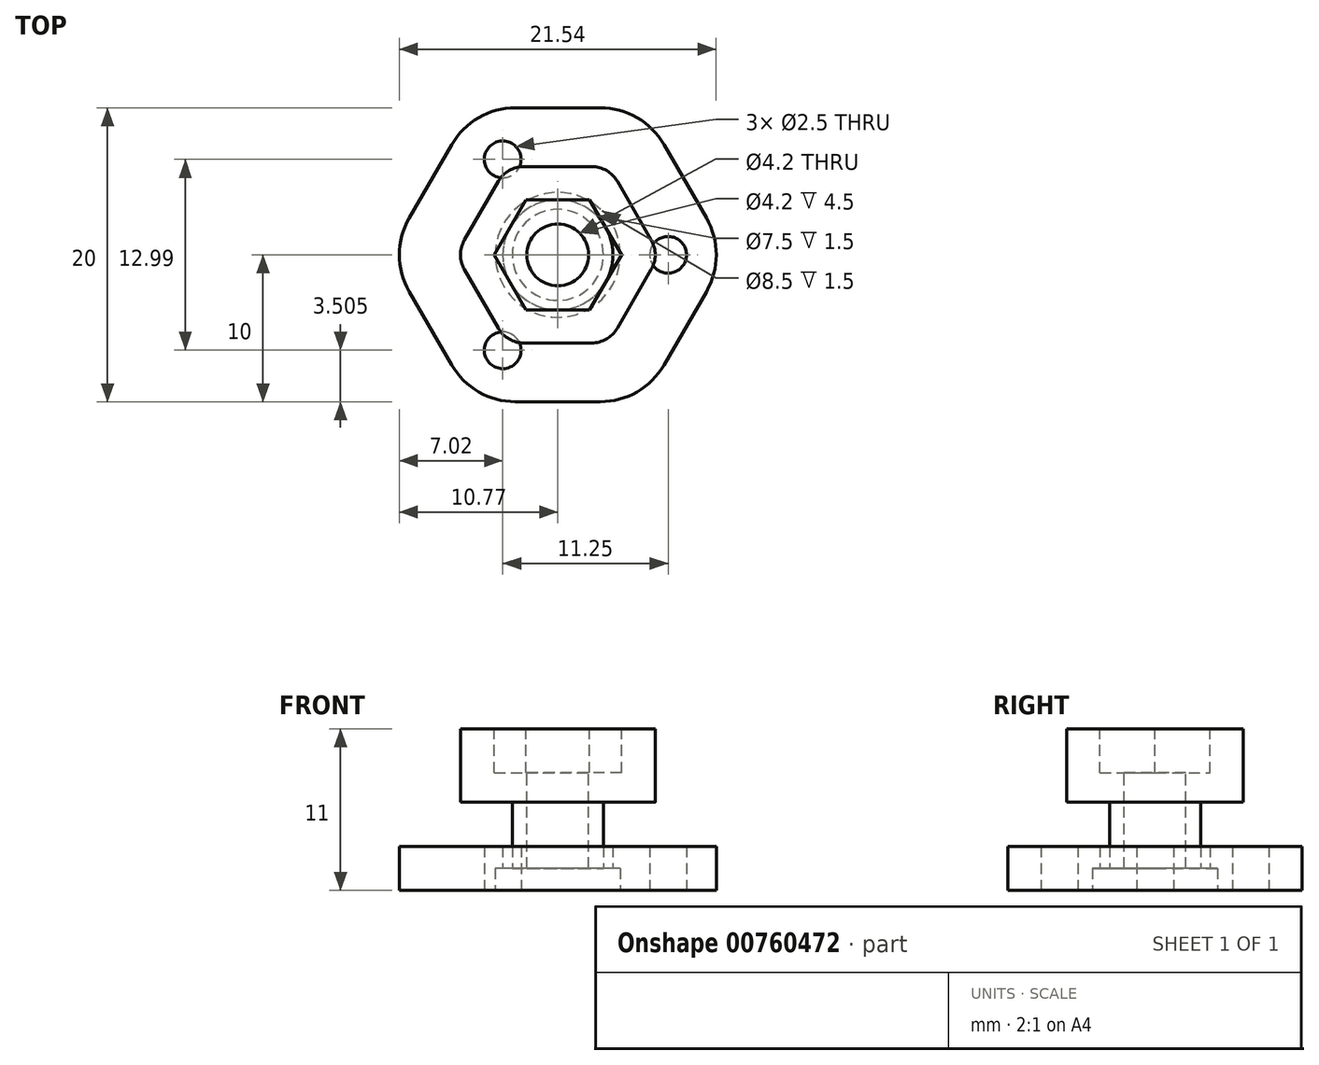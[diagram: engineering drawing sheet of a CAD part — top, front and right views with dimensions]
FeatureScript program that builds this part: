
annotation { "Feature Type Name" : "Feature", "Feature Type Description" : "" }
export const myFeature = defineFeature(function(context is Context, id is Id, definition is map)
    precondition{}
    {
        {
            var Q0;
            Q0=qCreatedBy(makeId("Top.planeOp"),FACE);
            var sketch = newSketch(context, id + "F0", { "sketchPlane" : qUnion([Q0])});
            skCircle(sketch, "E0.cCircle", {"center": v(0, 0) * mm, "radius": 10 * mm, "construction": true});
            skLineSegment(sketch, "E0.0", {"start": v(-5.77, 10) * mm, "end": v(5.77, 10) * mm});
            skLineSegment(sketch, "E0.1", {"start": v(5.77, 10) * mm, "end": v(11.55, 0) * mm});
            skLineSegment(sketch, "E0.2", {"start": v(11.55, 0) * mm, "end": v(5.77, -10) * mm});
            skLineSegment(sketch, "E0.3", {"start": v(5.77, -10) * mm, "end": v(-5.77, -10) * mm});
            skLineSegment(sketch, "E0.4", {"start": v(-5.77, -10) * mm, "end": v(-11.55, 0) * mm});
            skLineSegment(sketch, "E0.5", {"start": v(-11.55, 0) * mm, "end": v(-5.77, 10) * mm});
            skPoint(sketch, "E0.0.midPoint", {"position": v(0, 10) * mm});
            skCircle(sketch, "E1", {"center": v(0, 0) * mm, "radius": 4.25 * mm});
            skCircle(sketch, "E2", {"center": v(0, 0) * mm, "radius": 3.75 * mm});
            skCircle(sketch, "E3", {"center": v(7.5, 0) * mm, "radius": 1.25 * mm});
            skCircle(sketch, "E4.1.0", {"center": v(-3.75, 6.5) * mm, "radius": 1.25 * mm});
            skCircle(sketch, "E4.2.0", {"center": v(-3.75, -6.5) * mm, "radius": 1.25 * mm});
            skSolve(sketch);
        }
        {
            var Q0;
            Q0=makeQuery(id+"F0.imprint","IMPRINT",FACE,{"disambiguationData":[TD([[makeQuery(id+"F0.imprint","IMPRINT",EDGE,{"derivedFrom":sQuery(id+"F0.wireOp",EDGE,"E0.0")}),-1.0]])]});
            var Q1;
            Q1=makeQuery(id+"F0.imprint","IMPRINT",FACE,{"disambiguationData":[TD([[makeQuery(id+"F0.imprint","IMPRINT",EDGE,{"derivedFrom":sQuery(id+"F0.wireOp",EDGE,"E1")}),1.0]])]});
            extrude(context, id + "F1", {"entities" : qUnion([Q0, Q1]), "depth" : 3 * mm, "offsetDistance" : 25 * mm});
        }
        {
            var Q0;
            Q0=makeQuery(id+"F0.imprint","IMPRINT",FACE,{"disambiguationData":[TD([[makeQuery(id+"F0.imprint","IMPRINT",EDGE,{"derivedFrom":sQuery(id+"F0.wireOp",EDGE,"E1")}),1.0]])]});
            extrude(context, id + "F2", {"entities" : qUnion([Q0]), "operationType" : NewBodyOperationType.REMOVE, "depth" : 1.5 * mm, "offsetDistance" : 25 * mm});
        }
        {
            var Q0;
            Q0=makeQuery(id+"F1.opExtrude","SWEPT_EDGE",EDGE,{"disambiguationData":[OSD([sQuery(id+"F0.wireOp",EDGE,"E0.2"),sQuery(id+"F0.wireOp",EDGE,"E0.3")])]});
            var Q1;
            Q1=makeQuery(id+"F1.opExtrude","SWEPT_EDGE",EDGE,{"disambiguationData":[OSD([sQuery(id+"F0.wireOp",EDGE,"E0.1"),sQuery(id+"F0.wireOp",EDGE,"E0.2")])]});
            var Q2;
            Q2=makeQuery(id+"F1.opExtrude","SWEPT_EDGE",EDGE,{"disambiguationData":[OSD([sQuery(id+"F0.wireOp",EDGE,"E0.3"),sQuery(id+"F0.wireOp",EDGE,"E0.4")])]});
            var Q3;
            Q3=makeQuery(id+"F1.opExtrude","SWEPT_EDGE",EDGE,{"disambiguationData":[OSD([sQuery(id+"F0.wireOp",EDGE,"E0.4"),sQuery(id+"F0.wireOp",EDGE,"E0.5")])]});
            var Q4;
            Q4=makeQuery(id+"F1.opExtrude","SWEPT_EDGE",EDGE,{"disambiguationData":[OSD([sQuery(id+"F0.wireOp",EDGE,"E0.0"),sQuery(id+"F0.wireOp",EDGE,"E0.5")])]});
            var Q5;
            Q5=makeQuery(id+"F1.opExtrude","SWEPT_EDGE",EDGE,{"disambiguationData":[OSD([sQuery(id+"F0.wireOp",EDGE,"E0.0"),sQuery(id+"F0.wireOp",EDGE,"E0.1")])]});
            fillet(context, id + "F3", {"entities" : qUnion([Q0, Q1, Q2, Q3, Q4, Q5]), "radius" : 5 * mm, "tangentPropagation" : true, "allowEdgeOverflow" : false});
        }
        {
            var Q0;
            Q0=makeQuery(id+"F2.boolean.opBoolean","COPY",FACE,{"derivedFrom":makeQuery(id+"F2.opExtrude","CAP_FACE",FACE,{"disambiguationData":[OSD([sQuery(id+"F0.wireOp",EDGE,"E1"),sQuery(id+"F0.wireOp",EDGE,"E2")])],"isStart":false})});
            var sketch = newSketch(context, id + "F4", { "sketchPlane" : qUnion([Q0])});
            skCircle(sketch, "E5", {"center": v(0, 0) * mm, "radius": 3.1 * mm});
            skSolve(sketch);
        }
        {
            var Q0;
            Q0 = qSketchRegion(id + "F4", true);
            extrude(context, id + "F5", {"entities" : qUnion([Q0]), "oppositeDirection" : true, "depth" : 4.5 * mm, "offsetDistance" : 25 * mm});
        }
        {
            var Q0;
            Q0=makeQuery(id+"F5.opExtrude","CAP_FACE",FACE,{"disambiguationData":[OSD([sQuery(id+"F4.wireOp",EDGE,"E5")])],"isStart":false});
            var sketch = newSketch(context, id + "F6", { "sketchPlane" : qUnion([Q0])});
            skCircle(sketch, "E6.cCircle", {"center": v(0, 0) * mm, "radius": 6 * mm, "construction": true});
            skLineSegment(sketch, "E6.0", {"start": v(-3.46, 6) * mm, "end": v(3.46, 6) * mm});
            skLineSegment(sketch, "E6.1", {"start": v(3.46, 6) * mm, "end": v(6.93, 0) * mm});
            skLineSegment(sketch, "E6.2", {"start": v(6.93, 0) * mm, "end": v(3.46, -6) * mm});
            skLineSegment(sketch, "E6.3", {"start": v(3.46, -6) * mm, "end": v(-3.46, -6) * mm});
            skLineSegment(sketch, "E6.4", {"start": v(-3.46, -6) * mm, "end": v(-6.93, 0) * mm});
            skLineSegment(sketch, "E6.5", {"start": v(-6.93, 0) * mm, "end": v(-3.46, 6) * mm});
            skPoint(sketch, "E6.0.midPoint", {"position": v(0, 6) * mm});
            skSolve(sketch);
        }
        {
            var Q0;
            Q0 = qSketchRegion(id + "F6", true);
            extrude(context, id + "F7", {"entities" : qUnion([Q0]), "depth" : 5 * mm, "offsetDistance" : 25 * mm});
        }
        {
            var Q0;
            Q0=makeQuery(id+"F7.opExtrude","CAP_FACE",FACE,{"disambiguationData":[OSD([sQuery(id+"F6.wireOp",EDGE,"E6.0"),sQuery(id+"F6.wireOp",EDGE,"E6.1"),sQuery(id+"F6.wireOp",EDGE,"E6.2"),sQuery(id+"F6.wireOp",EDGE,"E6.3"),sQuery(id+"F6.wireOp",EDGE,"E6.4"),sQuery(id+"F6.wireOp",EDGE,"E6.5")])],"isStart":false});
            var sketch = newSketch(context, id + "F8", { "sketchPlane" : qUnion([Q0])});
            skCircle(sketch, "E7", {"center": v(0, 0) * mm, "radius": 2.1 * mm});
            skCircle(sketch, "E8.cCircle", {"center": v(0, 0) * mm, "radius": 3.75 * mm, "construction": true});
            skLineSegment(sketch, "E8.0", {"start": v(-2.17, 3.75) * mm, "end": v(2.17, 3.75) * mm});
            skLineSegment(sketch, "E8.1", {"start": v(2.17, 3.75) * mm, "end": v(4.33, 0) * mm});
            skLineSegment(sketch, "E8.2", {"start": v(4.33, 0) * mm, "end": v(2.17, -3.75) * mm});
            skLineSegment(sketch, "E8.3", {"start": v(2.17, -3.75) * mm, "end": v(-2.17, -3.75) * mm});
            skLineSegment(sketch, "E8.4", {"start": v(-2.17, -3.75) * mm, "end": v(-4.33, 0) * mm});
            skLineSegment(sketch, "E8.5", {"start": v(-4.33, 0) * mm, "end": v(-2.17, 3.75) * mm});
            skPoint(sketch, "E8.0.midPoint", {"position": v(0, 3.75) * mm});
            skSolve(sketch);
        }
        {
            var Q0;
            Q0=makeQuery(id+"F8.imprint","IMPRINT",FACE,{"disambiguationData":[TD([[makeQuery(id+"F8.imprint","IMPRINT",EDGE,{"derivedFrom":sQuery(id+"F8.wireOp",EDGE,"E7")}),-1.0]])]});
            var Q1;
            Q1=makeQuery(id+"F8.imprint","IMPRINT",FACE,{"disambiguationData":[TD([[makeQuery(id+"F8.imprint","IMPRINT",EDGE,{"derivedFrom":sQuery(id+"F8.wireOp",EDGE,"E7")}),1.0]])]});
            extrude(context, id + "F9", {"entities" : qUnion([Q0, Q1]), "operationType" : NewBodyOperationType.REMOVE, "oppositeDirection" : true, "depth" : 3 * mm, "offsetDistance" : 25 * mm});
        }
        {
            var Q0;
            Q0=makeQuery(id+"F8.imprint","IMPRINT",FACE,{"disambiguationData":[TD([[makeQuery(id+"F8.imprint","IMPRINT",EDGE,{"derivedFrom":sQuery(id+"F8.wireOp",EDGE,"E7")}),1.0]])]});
            extrude(context, id + "F10", {"entities" : qUnion([Q0]), "operationType" : NewBodyOperationType.REMOVE, "endBound" : BoundingType.THROUGH_ALL, "oppositeDirection" : true, "depth" : 25 * mm, "offsetDistance" : 25 * mm});
        }
        {
            var Q0;
            Q0=makeQuery(id+"F7.opExtrude","SWEPT_EDGE",EDGE,{"disambiguationData":[OSD([sQuery(id+"F6.wireOp",EDGE,"E6.1"),sQuery(id+"F6.wireOp",EDGE,"E6.2")])]});
            var Q1;
            Q1=makeQuery(id+"F7.opExtrude","SWEPT_EDGE",EDGE,{"disambiguationData":[OSD([sQuery(id+"F6.wireOp",EDGE,"E6.2"),sQuery(id+"F6.wireOp",EDGE,"E6.3")])]});
            var Q2;
            Q2=makeQuery(id+"F7.opExtrude","SWEPT_EDGE",EDGE,{"disambiguationData":[OSD([sQuery(id+"F6.wireOp",EDGE,"E6.3"),sQuery(id+"F6.wireOp",EDGE,"E6.4")])]});
            var Q3;
            Q3=makeQuery(id+"F7.opExtrude","SWEPT_EDGE",EDGE,{"disambiguationData":[OSD([sQuery(id+"F6.wireOp",EDGE,"E6.0"),sQuery(id+"F6.wireOp",EDGE,"E6.1")])]});
            var Q4;
            Q4=makeQuery(id+"F7.opExtrude","SWEPT_EDGE",EDGE,{"disambiguationData":[OSD([sQuery(id+"F6.wireOp",EDGE,"E6.0"),sQuery(id+"F6.wireOp",EDGE,"E6.5")])]});
            var Q5;
            Q5=makeQuery(id+"F7.opExtrude","SWEPT_EDGE",EDGE,{"disambiguationData":[OSD([sQuery(id+"F6.wireOp",EDGE,"E6.4"),sQuery(id+"F6.wireOp",EDGE,"E6.5")])]});
            fillet(context, id + "F11", {"entities" : qUnion([Q0, Q1, Q2, Q3, Q4, Q5]), "radius" : 2 * mm, "tangentPropagation" : true, "allowEdgeOverflow" : false});
        }
    });
